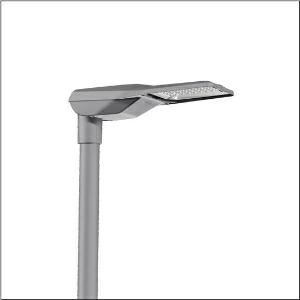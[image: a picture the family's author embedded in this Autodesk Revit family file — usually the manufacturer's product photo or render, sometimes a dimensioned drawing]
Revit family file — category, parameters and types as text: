
# Revit family: streetlight_sl_21_iq_mini___st0_5a_5xe2b41g08jb_20f7
name_source: partatom
category: Lighting Fixtures
units: mm (PartAtom-declared; Revit-internal decimal feet)

## family parameters
Cut with Voids When Loaded = No
Host = Face
Light Source = No
Part Type = Normal
Room Calculation Point = No
Round Connector Dimension = Use Diameter
Shared = No

## types (1)
- --- (1 x LED, 11290 lm, 71.6 W, 4000K)
    Apparent Load = 72 VA
    CIE Flux Codes = 43 76 97 100 100
    Color Rendering = 70
    Color Temperature = 4000K
    Default Elevation = 1800 mm
    Description = Streetlight SL 21 iQ mini, mast luminaire, primary light control with lens, of PMMA, primary optical cover: cover, of toughened safety glass, transparent, light distribution: ST0.5a, light emission: direct distribution, primary light characteristic: asymmetric, installation type: post-top, side-entry, LED, High Power LED, rated luminous flux: 11.290lm, luminous efficacy: 158lm/W, light colour: 740, colour temperature: 4000K, control: Street-Remote, Auto-Match, Temp-Guard, Lumen-Switch, Night-Set, Smart-Wire, Light-Fading, Desk-Remote (wireless, voltage-free reading and setting of iQ features in the workshop via application-optimized NFC function/RFID function), optimised constant luminous flux control (CLO 2.0), pre-setting: linear dimming characteristic, mains connection: 220..240V, AC, 50/60Hz, start of lifetime: 72W, end of service life: 75W, reduction: 33W, luminaire housing, of diecast aluminium, powder-coated, Siteco® metallic grey (DB 702S), corrosivity category C5 mid according to DIN EN ISO 12944, please order mast flange separately, inclination adjustable: 0°, 5°, 10°, 15°, sealing non-destructively replaceable, multi-level sealing system, length: 628mm, width: 235mm, height: 110mm, mast flange for spigot size: 42mm (side-entry): 5XC10008XM4, 60/48mm (side-entry/post-top): 5XC10108XM2, 76/60mm (side-entry/post-top): 5XC10108XM1, protection rating (complete): IP66, insulation class (complete): insulation class II (safety insulation), certification: CE, ENEC, ENEC+, VDE, impact resistance: IK09, permissible operating ambient temperature for outdoor applications: -40..+50°C, standard-compliant lighting for roads and squares, packaging unit: 1 piece

Light Distribution: ST0.5a
    Height = 110 mm
    Lamp = 1 x LED
    Lamp Light Flux = 11290 lm
    Lamp Power = 71.6 W
    Lamp count = 1
    Length = 625 mm
    Luminous efficacy = 158 lm/W
    Manufacturer = Siteco
    ModVariant = No
    Model = 5XE2B41G08JB
    Number of Poles = 1
    OnlyDefault = Yes
    Power Factor = 1
    Product Name = Streetlight SL 21 iQ mini | ST0.5a
    Product group = mast luminaire | pylon top
    ProductGroupID = 6100
    Protection Class = Protection class II
    Protection Degree = IP 66
    RLX_Detail_Level = 1
    RLX_Emergency_Light_Flux = 0 lm
    RLX_Emergency_Type = 0
    RLX_Emergency_Type_DB = No
    RlxData = <blob elided: 103513 chars, md5=3a9eaa2b>
    Socket = socket
    Standby Power = 0 W
    System Light Flux = 11290 lm
    System Power = 72 W
    Type Comments = factory setting: luminous flux: 100 % | dim-lin: 254 | 746 mA
    Type Image = l_1003519.jpg
    URL = http://relux.com
    VarID = @adj_142811
    Voltage = 0 V
    Weight = 0.00 kg
    Width = 234 mm

## geometry (parser evidence)
native form markers: Blend x4, Sweep x10
no freeform markers — native parametric forms only
